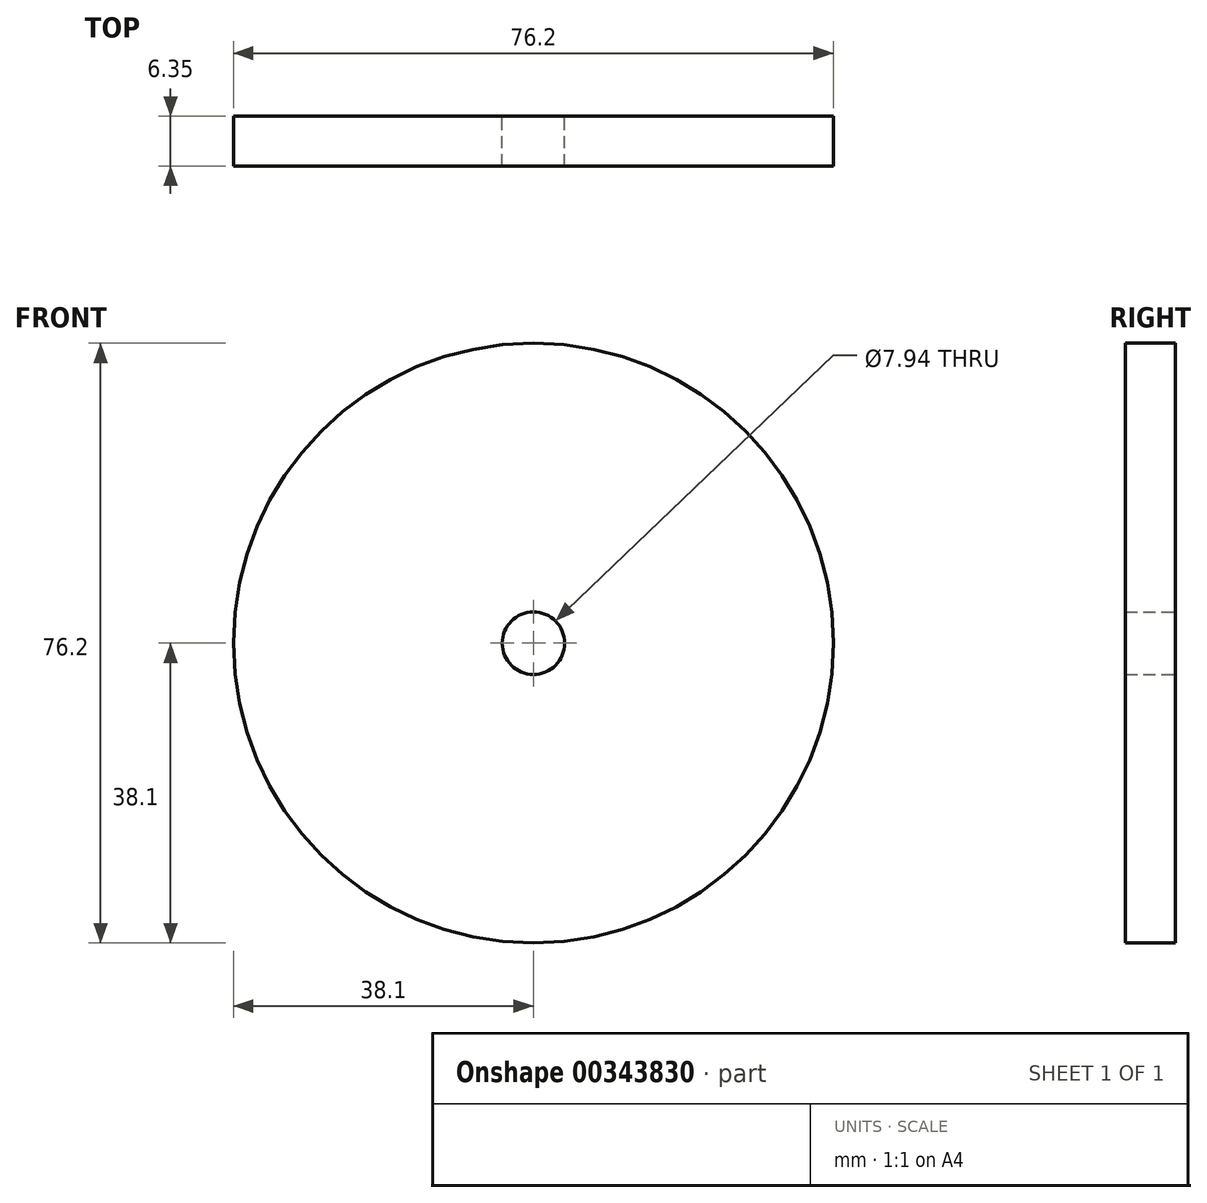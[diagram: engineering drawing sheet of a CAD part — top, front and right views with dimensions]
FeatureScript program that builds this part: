
annotation { "Feature Type Name" : "Feature", "Feature Type Description" : "" }
export const myFeature = defineFeature(function(context is Context, id is Id, definition is map)
    precondition{}
    {
        {
            var Q0;
            Q0=qCreatedBy(makeId("Front.planeOp"),FACE);
            var sketch = newSketch(context, id + "F0", { "sketchPlane" : qUnion([Q0])});
            skCircle(sketch, "E0", {"center": v(0, 0) * mm, "radius": 3.97 * mm});
            skCircle(sketch, "E1", {"center": v(0, 0) * mm, "radius": 38.1 * mm});
            skSolve(sketch);
        }
        {
            var Q0;
            Q0 = qSketchRegion(id + "F0", true);
            extrude(context, id + "F1", {"entities" : qUnion([Q0]), "depth" : 6.35 * mm});
        }
    });
